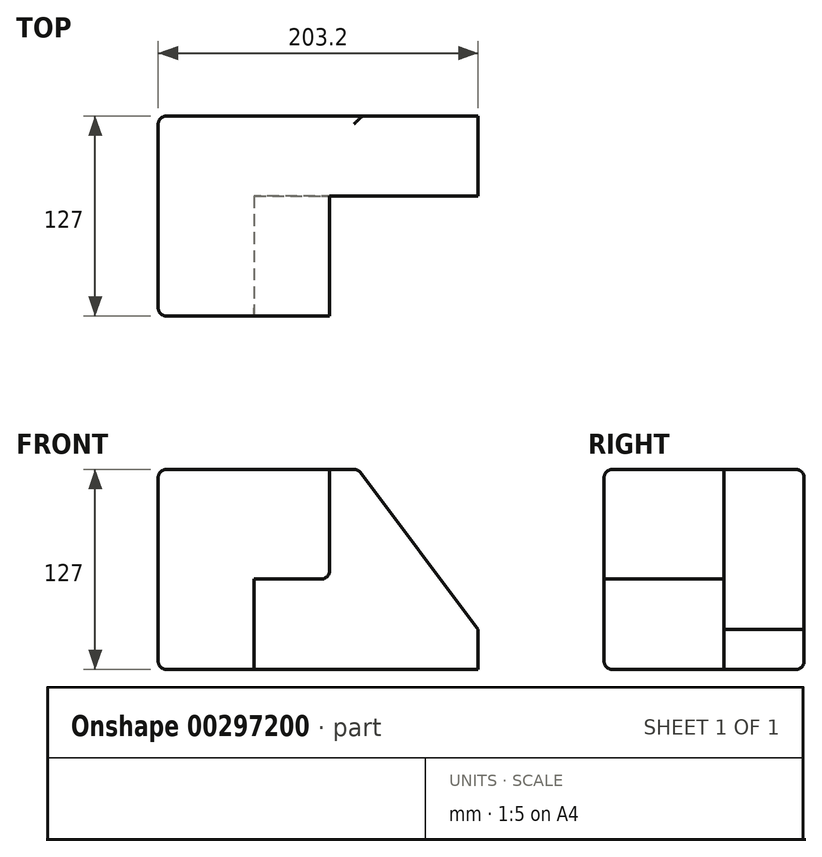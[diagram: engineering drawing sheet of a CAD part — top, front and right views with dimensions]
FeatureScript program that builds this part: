
annotation { "Feature Type Name" : "Feature", "Feature Type Description" : "" }
export const myFeature = defineFeature(function(context is Context, id is Id, definition is map)
    precondition{}
    {
        {
            var Q0;
            Q0=qCreatedBy(makeId("Front.planeOp"),FACE);
            var sketch = newSketch(context, id + "F0", { "sketchPlane" : qUnion([Q0])});
            skLineSegment(sketch, "E0.bottom", {"start": v(101.6, 63.5) * mm, "end": v(-101.6, 63.5) * mm});
            skLineSegment(sketch, "E0.top", {"start": v(101.6, -63.5) * mm, "end": v(-101.6, -63.5) * mm});
            skLineSegment(sketch, "E0.left", {"start": v(101.6, 63.5) * mm, "end": v(101.6, -63.5) * mm});
            skLineSegment(sketch, "E0.right", {"start": v(-101.6, 63.5) * mm, "end": v(-101.6, -63.5) * mm});
            skPoint(sketch, "E0.middle", {"position": v(0, 0) * mm});
            skSolve(sketch);
        }
        {
            var Q0;
            Q0=makeQuery(id+"F0.imprint","IMPRINT",FACE,{"disambiguationData":[TD([[makeQuery(id+"F0.imprint","IMPRINT",EDGE,{"derivedFrom":sQuery(id+"F0.wireOp",EDGE,"E0.bottom")}),1.0]])]});
            extrude(context, id + "F1", {"entities" : qUnion([Q0]), "depth" : 127 * mm});
        }
        {
            var Q0;
            Q0=makeQuery(id+"F1.opExtrude","CAP_FACE",FACE,{"disambiguationData":[OSD([sQuery(id+"F0.wireOp",EDGE,"E0.bottom"),sQuery(id+"F0.wireOp",EDGE,"E0.top"),sQuery(id+"F0.wireOp",EDGE,"E0.left"),sQuery(id+"F0.wireOp",EDGE,"E0.right")])],"isStart":false});
            var sketch = newSketch(context, id + "F2", { "sketchPlane" : qUnion([Q0])});
            skLineSegment(sketch, "E1", {"start": v(-40.64, -63.5) * mm, "end": v(-40.64, -6.08) * mm});
            skLineSegment(sketch, "E2", {"start": v(-40.64, -6.08) * mm, "end": v(7.12, -6.08) * mm});
            skLineSegment(sketch, "E3", {"start": v(7.12, -6.08) * mm, "end": v(7.12, 63.5) * mm});
            skSolve(sketch);
        }
        {
            var Q0;
            {var subQ2=sQuery(id+"F2.wireOp",EDGE,"E1");Q0=makeQuery(id+"F2.imprint","IMPRINT",FACE,{"disambiguationData":[TD([[makeQuery(id+"F2.imprint","IMPRINT",EDGE,{"derivedFrom":subQ2}),-1.0]])]});}
            extrude(context, id + "F3", {"entities" : qUnion([Q0]), "operationType" : NewBodyOperationType.REMOVE, "oppositeDirection" : true, "depth" : 76.2 * mm});
        }
        {
            var Q0;
            Q0=makeQuery(id+"F1.opExtrude","SWEPT_EDGE",EDGE,{"disambiguationData":[OSD([sQuery(id+"F0.wireOp",EDGE,"E0.bottom"),sQuery(id+"F0.wireOp",EDGE,"E0.left")])]});
            chamfer(context, id + "F4", {"entities" : qUnion([Q0]), "chamferType" : ChamferType.TWO_OFFSETS, "width1" : 76.2 * mm, "oppositeDirection" : false, "width2" : 101.6 * mm, "tangentPropagation" : true});
        }
        {
            var Q0;
            Q0=makeQuery(id+"F1.opExtrude","CAP_EDGE",EDGE,{"disambiguationData":[OSD([sQuery(id+"F0.wireOp",EDGE,"E0.bottom")])],"isStart":false});
            var Q1;
            Q1=makeQuery(id+"F3.boolean.opBoolean","COPY",EDGE,{"derivedFrom":makeQuery(id+"F3.opExtrude","CAP_EDGE",EDGE,{"disambiguationData":[OSD([sQuery(id+"F2.wireOp",EDGE,"E3")])],"isStart":true})});
            var Q2;
            Q2=makeQuery(id+"F3.boolean.opBoolean","COPY",EDGE,{"derivedFrom":makeQuery(id+"F3.opExtrude","SWEPT_EDGE",EDGE,{"disambiguationData":[OSD([sQuery(id+"F2.wireOp",EDGE,"E2"),sQuery(id+"F2.wireOp",EDGE,"E3")])]})});
            var Q3;
            Q3=makeQuery(id+"F3.boolean.opBoolean","COPY",EDGE,{"derivedFrom":makeQuery(id+"F3.opExtrude","SWEPT_EDGE",EDGE,{"disambiguationData":[OSD([sQuery(id+"F0.wireOp",EDGE,"E0.bottom"),sQuery(id+"F2.wireOp",EDGE,"E3")])]})});
            var Q4;
            Q4=makeQuery(id+"F3.boolean.opBoolean","COPY",EDGE,{"derivedFrom":makeQuery(id+"F3.opExtrude","CAP_EDGE",EDGE,{"disambiguationData":[OSD([sQuery(id+"F0.wireOp",EDGE,"E0.bottom")])],"isStart":false})});
            var Q5;
            {var subQ0=sQuery(id+"F0.wireOp",EDGE,"E0.bottom");Q5=makeQuery(id+"F4.opChamfer","BLEND_EDGE",EDGE,{"blendedFrom":[makeQuery(id+"F1.opExtrude","SWEPT_EDGE",EDGE,{"disambiguationData":[OSD([subQ0,sQuery(id+"F0.wireOp",EDGE,"E0.left")])]}),makeQuery(id+"F1.opExtrude","SWEPT_FACE",FACE,{"disambiguationData":[OSD([subQ0])]})],"blendedInto":[makeQuery(id+"F1.opExtrude","SWEPT_FACE",FACE,{"disambiguationData":[OSD([subQ0])]})]});}
            var Q6;
            Q6=makeQuery(id+"F3.boolean.opBoolean","COPY",EDGE,{"derivedFrom":makeQuery(id+"F3.opExtrude","CAP_EDGE",EDGE,{"disambiguationData":[OSD([sQuery(id+"F2.wireOp",EDGE,"E2")])],"isStart":true})});
            var Q7;
            Q7=makeQuery(id+"F3.boolean.opBoolean","COPY",EDGE,{"derivedFrom":makeQuery(id+"F3.opExtrude","CAP_EDGE",EDGE,{"disambiguationData":[OSD([sQuery(id+"F2.wireOp",EDGE,"E1")])],"isStart":true})});
            var Q8;
            Q8=makeQuery(id+"F1.opExtrude","CAP_EDGE",EDGE,{"disambiguationData":[OSD([sQuery(id+"F0.wireOp",EDGE,"E0.top")])],"isStart":false});
            var Q9;
            Q9=makeQuery(id+"F1.opExtrude","CAP_EDGE",EDGE,{"disambiguationData":[OSD([sQuery(id+"F0.wireOp",EDGE,"E0.right")])],"isStart":false});
            var Q10;
            Q10=makeQuery(id+"F1.opExtrude","SWEPT_EDGE",EDGE,{"disambiguationData":[OSD([sQuery(id+"F0.wireOp",EDGE,"E0.bottom"),sQuery(id+"F0.wireOp",EDGE,"E0.right")])]});
            var Q11;
            Q11=makeQuery(id+"F1.opExtrude","SWEPT_EDGE",EDGE,{"disambiguationData":[OSD([sQuery(id+"F0.wireOp",EDGE,"E0.top"),sQuery(id+"F0.wireOp",EDGE,"E0.right")])]});
            var Q12;
            Q12=makeQuery(id+"F1.opExtrude","CAP_EDGE",EDGE,{"disambiguationData":[OSD([sQuery(id+"F0.wireOp",EDGE,"E0.right")])],"isStart":true});
            var Q13;
            Q13=makeQuery(id+"F1.opExtrude","CAP_EDGE",EDGE,{"disambiguationData":[OSD([sQuery(id+"F0.wireOp",EDGE,"E0.bottom")])],"isStart":true});
            var Q14;
            Q14=makeQuery(id+"F1.opExtrude","CAP_EDGE",EDGE,{"disambiguationData":[OSD([sQuery(id+"F0.wireOp",EDGE,"E0.top")])],"isStart":true});
            fillet(context, id + "F5", {"entities" : qUnion([Q0, Q1, Q2, Q3, Q4, Q5, Q6, Q7, Q8, Q9, Q10, Q11, Q12, Q13, Q14]), "radius" : 5.08 * mm, "tangentPropagation" : true, "allowEdgeOverflow" : false});
        }
        {
            var Q0;
            Q0=makeQuery(id+"F3.boolean.opBoolean","COPY",FACE,{"derivedFrom":makeQuery(id+"F3.opExtrude","CAP_FACE",FACE,{"disambiguationData":[OSD([sQuery(id+"F0.wireOp",EDGE,"E0.bottom"),sQuery(id+"F0.wireOp",EDGE,"E0.top"),sQuery(id+"F0.wireOp",EDGE,"E0.left"),sQuery(id+"F2.wireOp",EDGE,"E1"),sQuery(id+"F2.wireOp",EDGE,"E2"),sQuery(id+"F2.wireOp",EDGE,"E3")])],"isStart":false})});
            var sketch = newSketch(context, id + "F6", { "sketchPlane" : qUnion([Q0])});
            skCircle(sketch, "E4", {"center": v(15.84, -21.7) * mm, "radius": 15.24 * mm});
            skSolve(sketch);
        }
        {
            var Q0;
            Q0=sQuery(id+"F6.wireOp",EDGE,"E4");
            extrude(context, id + "F7", {"bodyType" : ToolBodyType.SURFACE, "surfaceEntities" : qUnion([Q0]), "depth" : 25.4 * mm});
        }
    });
